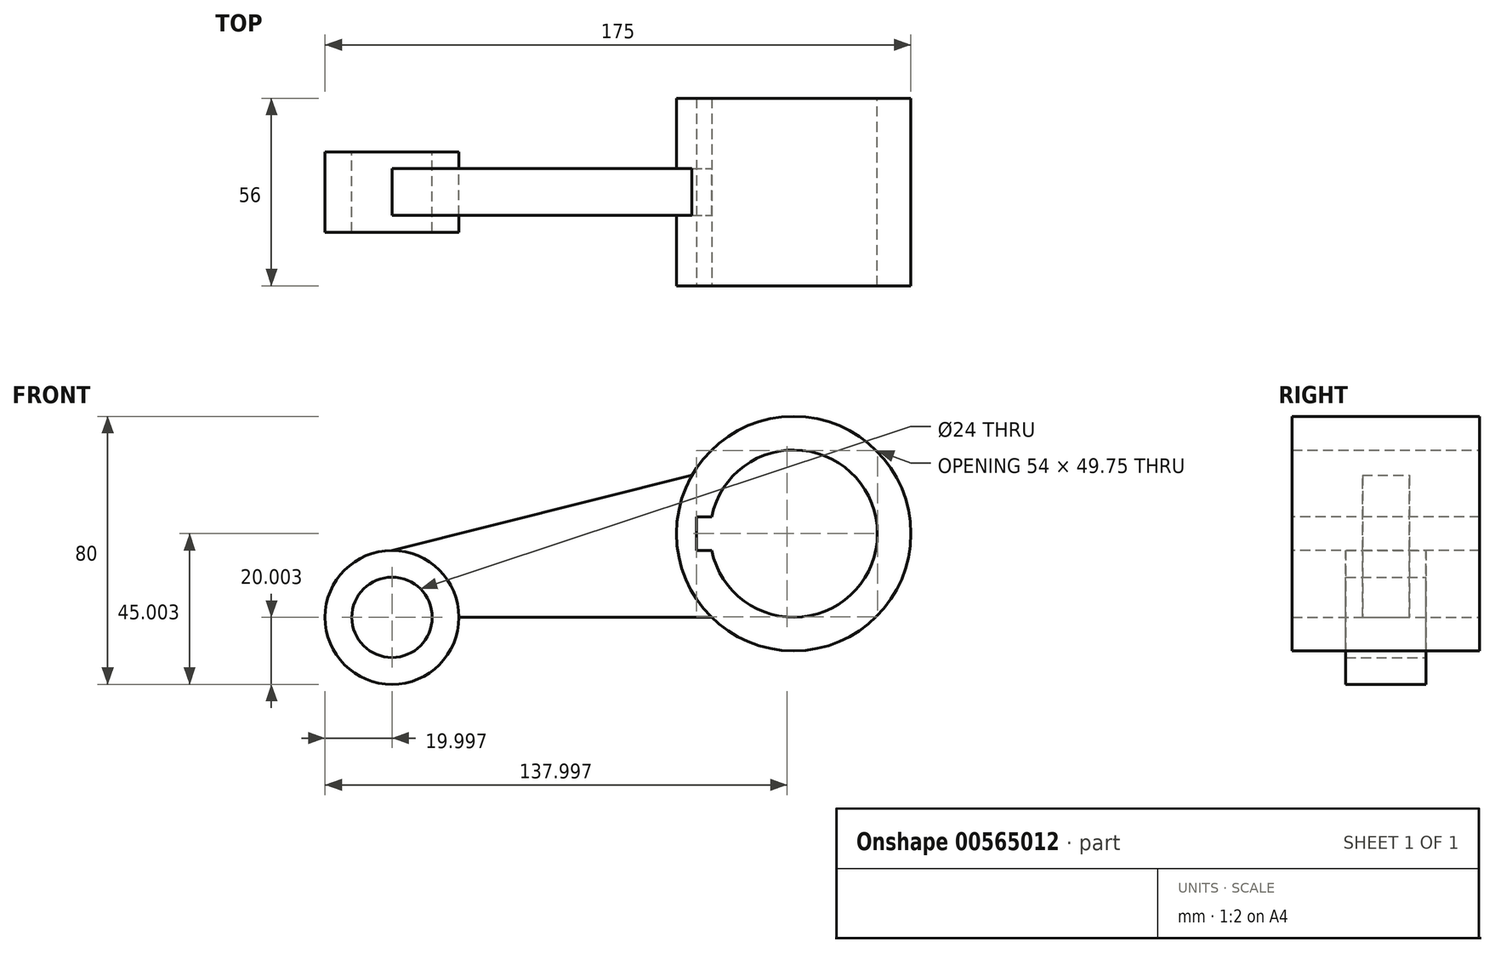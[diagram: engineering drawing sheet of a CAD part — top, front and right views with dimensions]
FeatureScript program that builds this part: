
annotation { "Feature Type Name" : "Feature", "Feature Type Description" : "" }
export const myFeature = defineFeature(function(context is Context, id is Id, definition is map)
    precondition{}
    {
        {
            var Q0;
            Q0=qCreatedBy(makeId("Front.planeOp"),FACE);
            var sketch = newSketch(context, id + "F0", { "sketchPlane" : qUnion([Q0])});
            skLineSegment(sketch, "E0", {"start": v(-62.54, -20.7) * mm, "end": v(32.96, -20.7) * mm});
            skCircle(sketch, "E1", {"center": v(-62.54, -20.7) * mm, "radius": 12 * mm});
            skCircle(sketch, "E2", {"center": v(-62.54, -20.7) * mm, "radius": 20 * mm});
            skLineSegment(sketch, "E3", {"start": v(-62.54, -0.7) * mm, "end": v(27.1, 21.7) * mm});
            skCircle(sketch, "E4", {"center": v(57.46, 4.3) * mm, "radius": 35 * mm});
            skCircle(sketch, "E5", {"center": v(57.46, 4.3) * mm, "radius": 25 * mm});
            skPoint(sketch, "E6.orphan", {"position": v(57.46, 29.3) * mm});
            skPoint(sketch, "E7.orphan", {"position": v(57.46, -20.7) * mm});
            skLineSegment(sketch, "E8", {"start": v(57.46, 29.3) * mm, "end": v(57.46, -20.7) * mm});
            skLineSegment(sketch, "E9", {"start": v(57.46, 4.3) * mm, "end": v(32.46, 4.3) * mm});
            skSolve(sketch);
        }
        {
            var Q0;
            {var subQ5=sQuery(id+"F0.wireOp",EDGE,"E3");Q0=makeQuery(id+"F0.imprint","IMPRINT",FACE,{"disambiguationData":[TD([[makeQuery(id+"F0.imprint","IMPRINT",EDGE,{"derivedFrom":subQ5}),-1.0]])]});}
            extrude(context, id + "F1", {"entities" : qUnion([Q0]), "depth" : 7 * mm, "offsetDistance" : 25 * mm, "hasSecondDirection" : true, "secondDirectionOppositeDirection" : true, "secondDirectionDepth" : 7 * mm});
        }
        {
            var Q0;
            Q0=makeQuery(id+"F0.imprint","IMPRINT",FACE,{"disambiguationData":[TD([[makeQuery(id+"F0.imprint","IMPRINT",EDGE,{"derivedFrom":sQuery(id+"F0.wireOp",EDGE,"E1")}),-1.0]])]});
            extrude(context, id + "F2", {"entities" : qUnion([Q0]), "operationType" : NewBodyOperationType.ADD, "depth" : 12 * mm, "offsetDistance" : 25 * mm, "hasSecondDirection" : true, "secondDirectionOppositeDirection" : true, "secondDirectionDepth" : 12 * mm});
        }
        {
            var Q0;
            Q0=makeQuery(id+"F0.imprint","IMPRINT",FACE,{"disambiguationData":[TD([[makeQuery(id+"F0.imprint","IMPRINT",EDGE,{"derivedFrom":sQuery(id+"F0.wireOp",EDGE,"E5")}),-1.0]])]});
            extrude(context, id + "F3", {"entities" : qUnion([Q0]), "operationType" : NewBodyOperationType.ADD, "depth" : 28 * mm, "offsetDistance" : 25 * mm, "hasSecondDirection" : true, "secondDirectionOppositeDirection" : true, "secondDirectionDepth" : 28 * mm});
        }
        {
            var Q0;
            {var subQ5=sQuery(id+"F0.wireOp",EDGE,"E4");var subQ6=makeQuery(id+"F0.imprint","INTERSECT",VERTEX,{"derivedFrom":[sQuery(id+"F0.wireOp",EDGE,"E0"),subQ5]});Q0=makeQuery(id+"F0.imprint","IMPRINT",FACE,{"disambiguationData":[TD([[makeQuery(id+"F0.imprint","IMPRINT",EDGE,{"disambiguationData":[TD([[subQ6,1.0]])],"derivedFrom":subQ5}),1.0]])]});}
            var sketch = newSketch(context, id + "F4", { "sketchPlane" : qUnion([Q0])});
            skLineSegment(sketch, "E10.0.0", {"start": v(57.46, 4.3) * mm, "end": v(32.46, 4.3) * mm});
            skArc(sketch, "E10.0.1", {"start": v(32.46, 4.3) * mm, "mid": v(39.78, -13.38) * mm, "end": v(57.46, -20.7) * mm});
            skLineSegment(sketch, "E10.0.2", {"start": v(57.46, -20.7) * mm, "end": v(57.46, 4.3) * mm});
            skLineSegment(sketch, "E11.0.0", {"start": v(32.46, 4.3) * mm, "end": v(57.46, 4.3) * mm});
            skLineSegment(sketch, "E11.0.1", {"start": v(57.46, 4.3) * mm, "end": v(57.46, 29.3) * mm});
            skArc(sketch, "E11.0.2", {"start": v(57.46, 29.3) * mm, "mid": v(39.78, 21.97) * mm, "end": v(32.46, 4.3) * mm});
            skLineSegment(sketch, "E12", {"start": v(32.46, 4.3) * mm, "end": v(28.46, 4.3) * mm});
            skLineSegment(sketch, "E13", {"start": v(28.46, 4.3) * mm, "end": v(28.46, -0.7) * mm});
            skLineSegment(sketch, "E14", {"start": v(28.46, -0.7) * mm, "end": v(28.46, 9.3) * mm});
            skPoint(sketch, "E14.endSnap0", {"position": v(28.46, 1.8) * mm});
            skLineSegment(sketch, "E15", {"start": v(28.46, 9.3) * mm, "end": v(32.46, 9.3) * mm});
            skLineSegment(sketch, "E16", {"start": v(28.46, -0.7) * mm, "end": v(32.96, -0.7) * mm});
            skLineSegment(sketch, "E17", {"start": v(32.46, 9.3) * mm, "end": v(32.96, 9.3) * mm});
            skSolve(sketch);
        }
        {
            var Q0;
            {var subQ0=sQuery(id+"F4.wireOp",EDGE,"E12");Q0=makeQuery(id+"F4.imprint","IMPRINT",FACE,{"disambiguationData":[TD([[makeQuery(id+"F4.imprint","IMPRINT",EDGE,{"derivedFrom":subQ0}),1.0]])]});}
            extrude(context, id + "F5", {"entities" : qUnion([Q0]), "operationType" : NewBodyOperationType.REMOVE, "oppositeDirection" : true, "depth" : 57.4 * mm, "offsetDistance" : 25 * mm, "hasSecondDirection" : true, "secondDirectionOppositeDirection" : false, "secondDirectionDepth" : 40.2 * mm});
        }
        {
            var Q0;
            {var subQ2=sQuery(id+"F4.wireOp",EDGE,"E12");Q0=makeQuery(id+"F4.imprint","IMPRINT",FACE,{"disambiguationData":[TD([[makeQuery(id+"F4.imprint","IMPRINT",EDGE,{"derivedFrom":subQ2}),-1.0]])]});}
            extrude(context, id + "F6", {"entities" : qUnion([Q0]), "operationType" : NewBodyOperationType.REMOVE, "oppositeDirection" : true, "depth" : 102.2 * mm, "offsetDistance" : 25 * mm, "hasSecondDirection" : true, "secondDirectionOppositeDirection" : false, "secondDirectionDepth" : 32.7 * mm});
        }
    });
